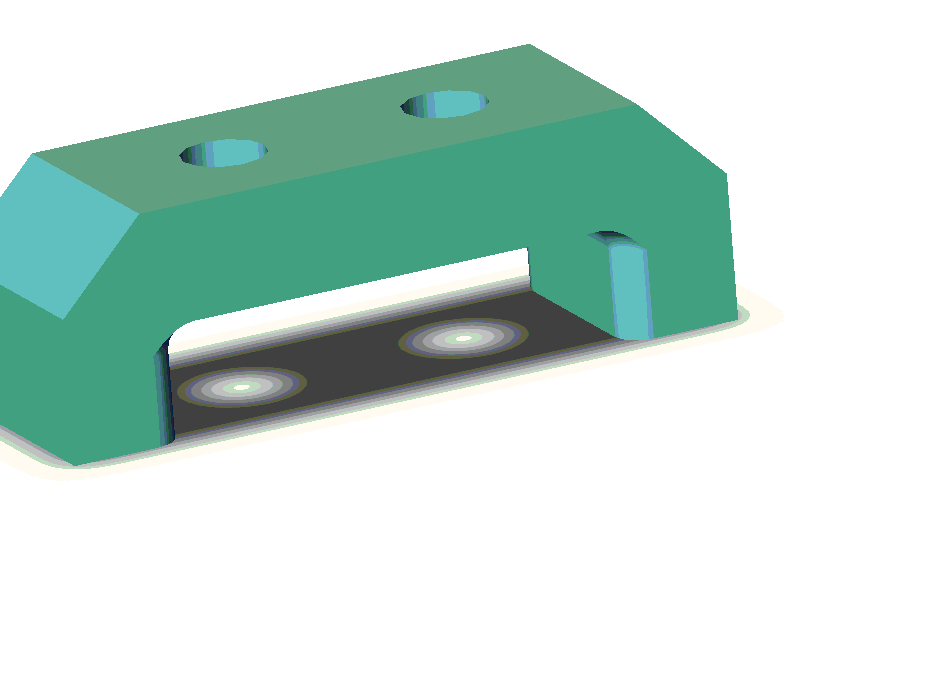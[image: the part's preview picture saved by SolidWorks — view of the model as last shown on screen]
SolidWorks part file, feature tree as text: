
SOLIDWORKS PART (.sldprt)
format: sldprt  version: not decoded by parser v0  size: 303,104 bytes
history: native  units: mm
features: fillet x3, sketch x2, extrude x1, cut_extrude x1, chamfer x1 (+8 scaffold rows collapsed)
feature tree (16):
  scaffold x8  (default folders/planes/origin — collapsed)
  sketch  "Sketch1"  dims[D1=38.1mm D2=12.7mm D3=6.35mm D4=6.35mm D5=6.35mm]
  extrude  "Base-Extrude"  Depth=12.7mm
  sketch  "Sketch2"  dims[D5=4.6228mm D6=4.6228mm D1=6.35mm D2=6.35mm D3=6.35mm D4=6.35mm]
  cut_extrude  "Cut-Extrude1"  Depth=19.859804mm
  chamfer  "Chamfer1"  Distance=4.7625mm Angle=45deg
  fillet  "Fillet2"  Radius=1.524mm
  fillet  "Fillet3"  Radius=1.524mm
  fillet  "Fillet4"  Radius=1.524mm
decode coverage: 8 of 8 modeling features carry decoded parameters
note: suppression state not decoded; provenance and decode notes live in map.json
